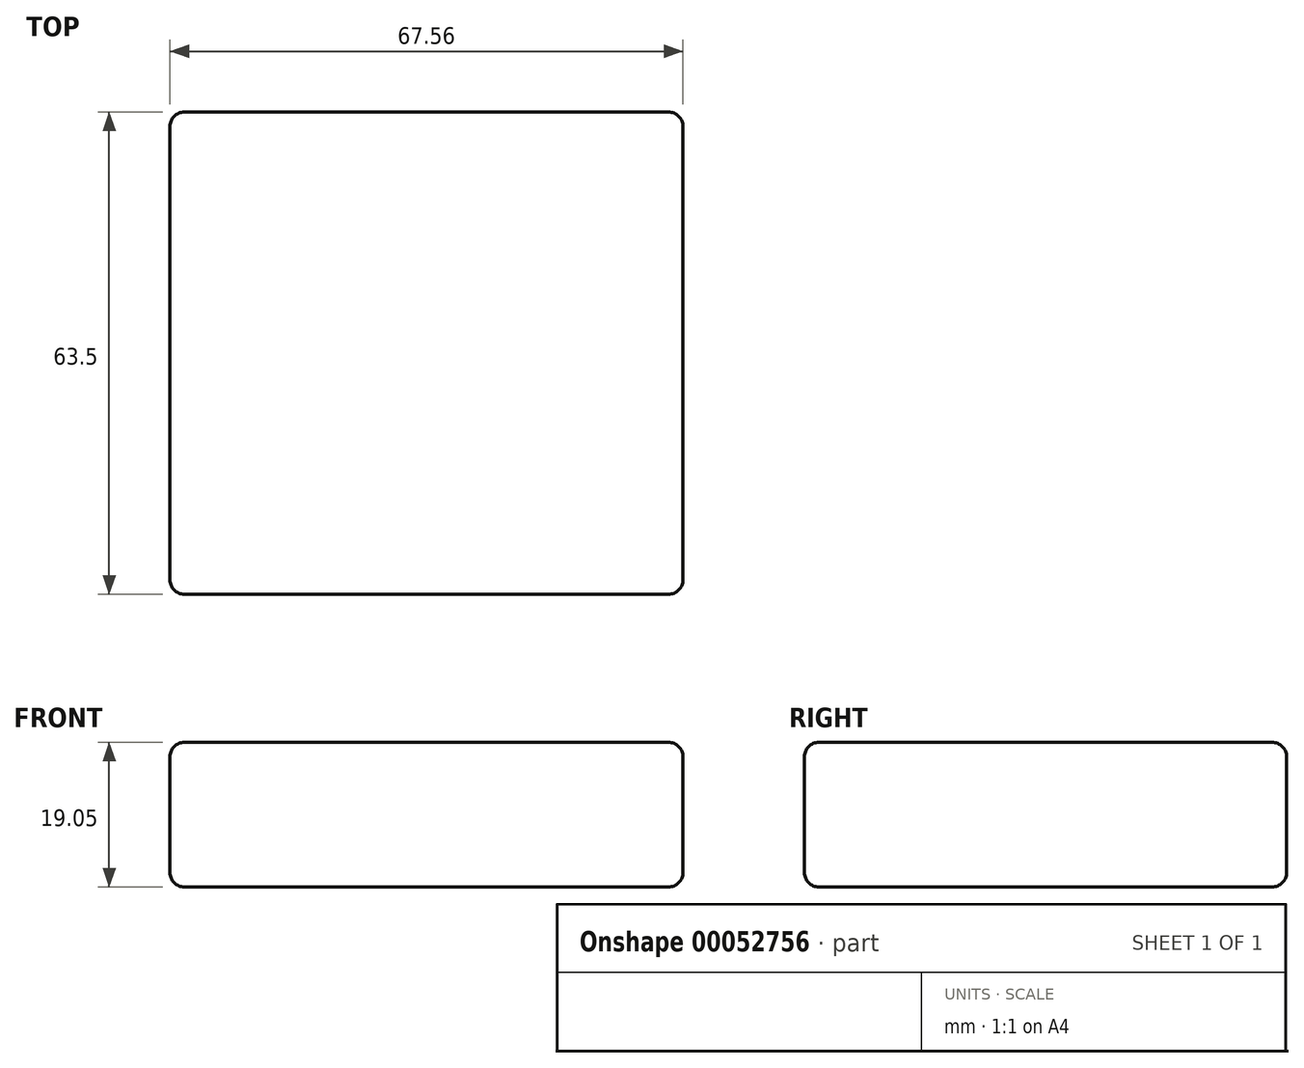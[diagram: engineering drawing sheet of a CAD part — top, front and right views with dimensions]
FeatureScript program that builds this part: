
annotation { "Feature Type Name" : "Feature", "Feature Type Description" : "" }
export const myFeature = defineFeature(function(context is Context, id is Id, definition is map)
    precondition{}
    {
        {
            var Q0;
            Q0=qCreatedBy(makeId("Top.planeOp"),FACE);
            var sketch = newSketch(context, id + "F0", { "sketchPlane" : qUnion([Q0])});
            skLineSegment(sketch, "E0.bottom", {"start": v(-33.78, 31.75) * mm, "end": v(33.78, 31.75) * mm});
            skLineSegment(sketch, "E0.top", {"start": v(-33.78, -31.75) * mm, "end": v(33.78, -31.75) * mm});
            skLineSegment(sketch, "E0.left", {"start": v(-33.78, 31.75) * mm, "end": v(-33.78, -31.75) * mm});
            skLineSegment(sketch, "E0.right", {"start": v(33.78, 31.75) * mm, "end": v(33.78, -31.75) * mm});
            skLineSegment(sketch, "E1", {"start": v(-33.78, 31.75) * mm, "end": v(33.78, -31.75) * mm, "construction": true});
            skSolve(sketch);
        }
        {
            var Q0;
            Q0 = qSketchRegion(id + "F0", true);
            extrude(context, id + "F1", {"entities" : qUnion([Q0]), "depth" : 19.05 * mm});
        }
        {
            var Q0;
            Q0=makeQuery(id+"F1.opExtrude","CAP_FACE",FACE,{"disambiguationData":[OSD([sQuery(id+"F0.wireOp",EDGE,"E0.bottom"),sQuery(id+"F0.wireOp",EDGE,"E0.top"),sQuery(id+"F0.wireOp",EDGE,"E0.left"),sQuery(id+"F0.wireOp",EDGE,"E0.right")])],"isStart":false});
            var Q1;
            Q1=makeQuery(id+"F1.opExtrude","CAP_FACE",FACE,{"disambiguationData":[OSD([sQuery(id+"F0.wireOp",EDGE,"E0.bottom"),sQuery(id+"F0.wireOp",EDGE,"E0.top"),sQuery(id+"F0.wireOp",EDGE,"E0.left"),sQuery(id+"F0.wireOp",EDGE,"E0.right")])],"isStart":true});
            var Q2;
            Q2=makeQuery(id+"F1.opExtrude","SWEPT_EDGE",EDGE,{"disambiguationData":[OSD([sQuery(id+"F0.wireOp",EDGE,"E0.bottom"),sQuery(id+"F0.wireOp",EDGE,"E0.right")])]});
            var Q3;
            Q3=makeQuery(id+"F1.opExtrude","SWEPT_EDGE",EDGE,{"disambiguationData":[OSD([sQuery(id+"F0.wireOp",EDGE,"E0.top"),sQuery(id+"F0.wireOp",EDGE,"E0.right")])]});
            var Q4;
            Q4=makeQuery(id+"F1.opExtrude","SWEPT_EDGE",EDGE,{"disambiguationData":[OSD([sQuery(id+"F0.wireOp",EDGE,"E0.top"),sQuery(id+"F0.wireOp",EDGE,"E0.left")])]});
            var Q5;
            Q5=makeQuery(id+"F1.opExtrude","SWEPT_EDGE",EDGE,{"disambiguationData":[OSD([sQuery(id+"F0.wireOp",EDGE,"E0.bottom"),sQuery(id+"F0.wireOp",EDGE,"E0.left")])]});
            fillet(context, id + "F2", {"entities" : qUnion([Q0, Q1, Q2, Q3, Q4, Q5]), "radius" : 1.9 * mm, "tangentPropagation" : true, "allowEdgeOverflow" : false});
        }
    });
